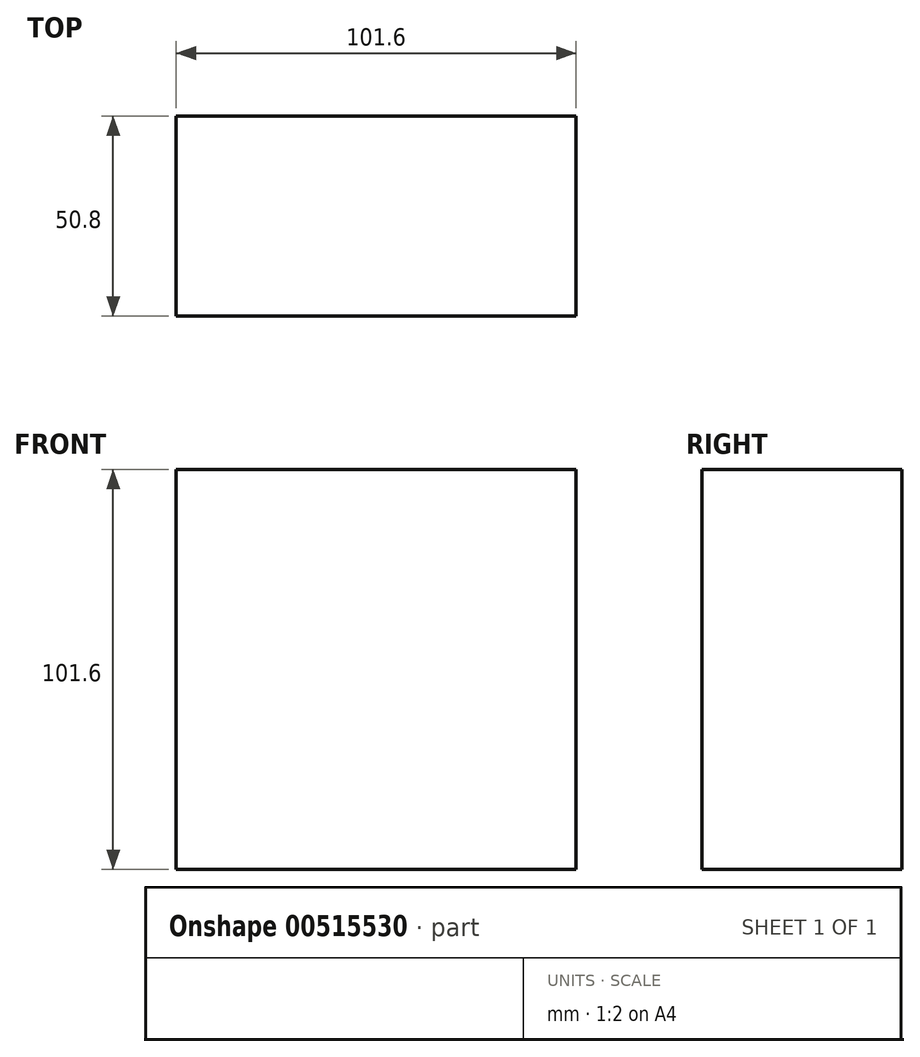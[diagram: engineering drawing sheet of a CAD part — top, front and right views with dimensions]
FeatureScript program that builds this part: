
annotation { "Feature Type Name" : "Feature", "Feature Type Description" : "" }
export const myFeature = defineFeature(function(context is Context, id is Id, definition is map)
    precondition{}
    {
        {
            var Q0;
            Q0=qCreatedBy(makeId("Right.planeOp"),FACE);
            var sketch = newSketch(context, id + "F0", { "sketchPlane" : qUnion([Q0])});
            skLineSegment(sketch, "E0.bottom", {"start": v(25.4, -50.8) * mm, "end": v(-25.4, -50.8) * mm});
            skLineSegment(sketch, "E0.top", {"start": v(25.4, 50.8) * mm, "end": v(-25.4, 50.8) * mm});
            skLineSegment(sketch, "E0.left", {"start": v(25.4, -50.8) * mm, "end": v(25.4, 50.8) * mm});
            skLineSegment(sketch, "E0.right", {"start": v(-25.4, -50.8) * mm, "end": v(-25.4, 50.8) * mm});
            skPoint(sketch, "E0.middle", {"position": v(0, 0) * mm});
            skSolve(sketch);
        }
        {
            var Q0;
            Q0=makeQuery(id+"F0.imprint","IMPRINT",FACE,{"disambiguationData":[TD([[makeQuery(id+"F0.imprint","IMPRINT",EDGE,{"derivedFrom":sQuery(id+"F0.wireOp",EDGE,"E0.bottom")}),-1.0]])]});
            extrude(context, id + "F1", {"entities" : qUnion([Q0]), "endBound" : BoundingType.SYMMETRIC, "depth" : 101.6 * mm, "offsetDistance" : 25.4 * mm});
        }
    });
